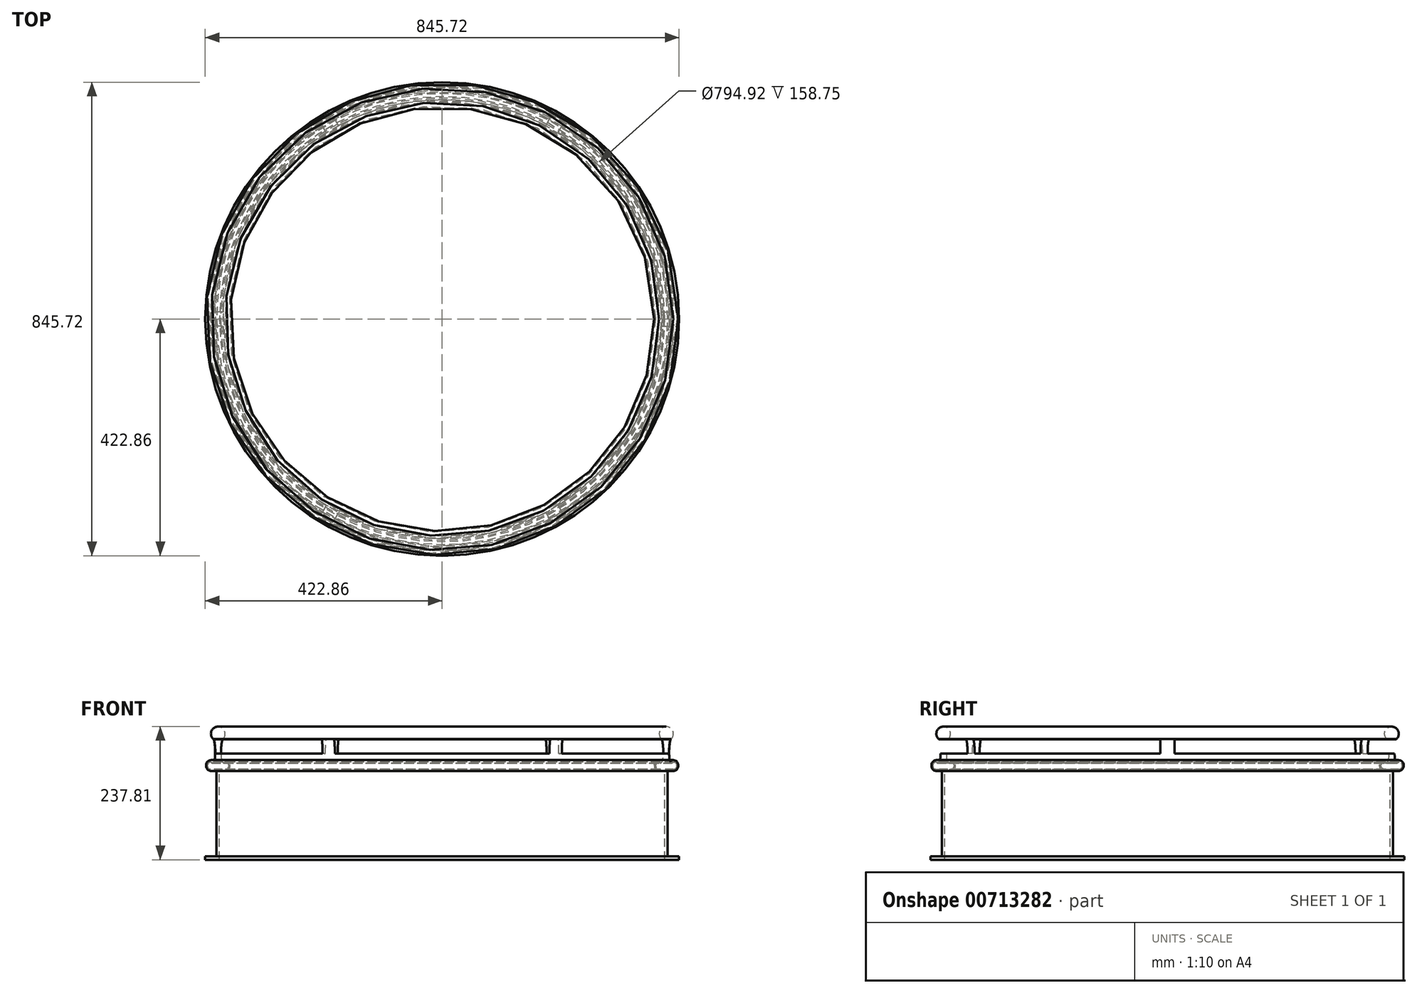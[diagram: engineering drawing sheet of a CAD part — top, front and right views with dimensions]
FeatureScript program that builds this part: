
annotation { "Feature Type Name" : "Feature", "Feature Type Description" : "" }
export const myFeature = defineFeature(function(context is Context, id is Id, definition is map)
    precondition{}
    {
        {
            var Q0;
            Q0=qCreatedBy(makeId("Front.planeOp"),FACE);
            var sketch = newSketch(context, id + "F0", { "sketchPlane" : qUnion([Q0])});
            skCircle(sketch, "E0", {"center": v(0, 0) * mm, "radius": 12.7 * mm});
            skLineSegment(sketch, "E1", {"start": v(0, -63.5) * mm, "end": v(-12.7, -63.5) * mm});
            skLineSegment(sketch, "E2", {"start": v(0, 0) * mm, "end": v(0, -63.5) * mm, "construction": true});
            skArc(sketch, "E3", {"start": v(-12.7, -50.8) * mm, "mid": v(-19.05, -57.15) * mm, "end": v(-12.7, -63.5) * mm});
            skFitSpline(sketch, "E4", {"points": [v(-12.7, -50.8) * mm, v(-9.63, -52.39) * mm, v(-6.21, -47.1) * mm, v(-8.6, -9.35) * mm], "startDerivative": vector(22.18, -25.1) * mm, "endDerivative": vector(-18.14, 18.14) * mm});
            skFitSpline(sketch, "E5", {"points": [v(-12.56, -50.43) * mm, v(-9.69, -51.96) * mm, v(-7.32, -49) * mm, v(-8.76, -47.55) * mm, v(-15.72, -47.83) * mm, v(-21.1, -53.83) * mm, v(-20.85, -60.48) * mm, v(-18.6, -64.21) * mm, v(-13.93, -66.36) * mm], "startDerivative": vector(26.86, -26.06) * mm, "endDerivative": vector(56.63, -6) * mm});
            skFitSpline(sketch, "E6", {"points": [v(-12.56, -50.43) * mm, v(-14.9, -50.8) * mm, v(-18.48, -53.57) * mm, v(-19.03, -59.46) * mm, v(-15.83, -63.1) * mm, v(-13.05, -63.82) * mm], "startDerivative": vector(-14.53, 0.11) * mm, "endDerivative": vector(20.5, -1.46) * mm});
            skLineSegment(sketch, "E7", {"start": v(-13.93, -66.36) * mm, "end": v(-2.54, -66.36) * mm});
            skLineSegment(sketch, "E8", {"start": v(-2.54, -66.36) * mm, "end": v(-2.54, -218.76) * mm});
            skLineSegment(sketch, "E9", {"start": v(-13.05, -63.82) * mm, "end": v(0, -63.82) * mm});
            skLineSegment(sketch, "E10", {"start": v(0, -58.82) * mm, "end": v(0, -76.45) * mm, "construction": true});
            skFitSpline(sketch, "E11.MirrorCS", {"points": [v(12.7, -50.8) * mm, v(9.63, -52.39) * mm, v(6.21, -47.1) * mm, v(8.6, -9.35) * mm], "startDerivative": vector(-22.18, -25.1) * mm, "endDerivative": vector(18.14, 18.14) * mm});
            skArc(sketch, "E12.MirrorCS", {"start": v(12.7, -50.8) * mm, "mid": v(19.05, -57.15) * mm, "end": v(12.7, -63.5) * mm});
            skFitSpline(sketch, "E13.MirrorCS", {"points": [v(12.56, -50.43) * mm, v(9.69, -51.96) * mm, v(7.32, -49) * mm, v(8.76, -47.55) * mm, v(15.72, -47.83) * mm, v(21.1, -53.83) * mm, v(20.85, -60.48) * mm, v(18.6, -64.21) * mm, v(13.93, -66.36) * mm], "startDerivative": vector(-26.86, -26.06) * mm, "endDerivative": vector(-56.63, -6) * mm});
            skLineSegment(sketch, "E14.MirrorCS", {"start": v(0, -63.5) * mm, "end": v(12.7, -63.5) * mm});
            skLineSegment(sketch, "E15.MirrorCS", {"start": v(13.05, -63.82) * mm, "end": v(0, -63.82) * mm});
            skLineSegment(sketch, "E16.MirrorCS", {"start": v(13.93, -66.36) * mm, "end": v(2.54, -66.36) * mm});
            skLineSegment(sketch, "E17.MirrorCS", {"start": v(2.54, -66.36) * mm, "end": v(2.54, -218.76) * mm});
            skFitSpline(sketch, "E18.MirrorCS", {"points": [v(12.56, -50.43) * mm, v(14.9, -50.8) * mm, v(18.48, -53.57) * mm, v(19.03, -59.46) * mm, v(15.83, -63.1) * mm, v(13.05, -63.82) * mm], "startDerivative": vector(14.53, 0.11) * mm, "endDerivative": vector(-20.5, -1.46) * mm});
            skLineSegment(sketch, "E19.top", {"start": v(2.54, -225.1) * mm, "end": v(-22.86, -225.1) * mm});
            skLineSegment(sketch, "E19.left", {"start": v(2.54, -218.76) * mm, "end": v(2.54, -225.1) * mm});
            skLineSegment(sketch, "E19.right", {"start": v(-22.86, -218.76) * mm, "end": v(-22.86, -225.1) * mm});
            skLineSegment(sketch, "E20.trimOffspring", {"start": v(-2.54, -218.76) * mm, "end": v(-22.86, -218.76) * mm});
            skSolve(sketch);
        }
        {
            var Q0;
            Q0=qCreatedBy(makeId("Right.planeOp"),FACE);
            cPlane(context, id + "F1", {"entities" : qUnion([Q0]), "cplaneType" : CPlaneType.OFFSET, "offset" : 400 * mm, "width" : 152.4 * mm, "height" : 152.4 * mm});
        }
        {
            var Q0;
            Q0=qCreatedBy(makeId("Front.planeOp"),FACE);
            var sketch = newSketch(context, id + "F2", { "sketchPlane" : qUnion([Q0])});
            skLineSegment(sketch, "E21", {"start": v(400, 76.37) * mm, "end": v(400, -72.94) * mm, "construction": true});
            skSolve(sketch);
        }
        {
            var Q0;
            Q0 = qSketchRegion(id + "F0", true);
            var Q1;
            Q1=sQuery(id+"F2.wireOp",EDGE,"E21");
            revolve(context, id + "F3", {"surfaceOperationType" : NewSurfaceOperationType.NEW, "entities" : qUnion([Q0]), "axis" : qUnion([Q1]), "revolveType" : RevolveType.FULL});
        }
        {
            var Q0;
            Q0=qCreatedBy(makeId("Top.planeOp"),FACE);
            cPlane(context, id + "F4", {"entities" : qUnion([Q0]), "cplaneType" : CPlaneType.OFFSET, "offset" : 10.16 * mm, "oppositeDirection" : true, "width" : 152.4 * mm, "height" : 152.4 * mm});
        }
        {
            var Q0;
            Q0=qCreatedBy(id+"F4.planeOp",FACE);
            var sketch = newSketch(context, id + "F5", { "sketchPlane" : qUnion([Q0])});
            skCircle(sketch, "E22.cCircle", {"center": v(400, 0) * mm, "radius": 439.94 * mm, "construction": true});
            skLineSegment(sketch, "E22.0", {"start": v(654, 439.94) * mm, "end": v(908, 0) * mm, "construction": true});
            skLineSegment(sketch, "E22.1", {"start": v(908, 0) * mm, "end": v(654, -439.94) * mm, "construction": true});
            skLineSegment(sketch, "E22.2", {"start": v(654, -439.94) * mm, "end": v(146, -439.94) * mm, "construction": true});
            skLineSegment(sketch, "E22.3", {"start": v(146, -439.94) * mm, "end": v(-108, 0) * mm, "construction": true});
            skLineSegment(sketch, "E22.4", {"start": v(-108, 0) * mm, "end": v(146, 439.94) * mm, "construction": true});
            skLineSegment(sketch, "E22.5", {"start": v(146, 439.94) * mm, "end": v(654, 439.94) * mm, "construction": true});
            skPoint(sketch, "E22.0.midPoint", {"position": v(781, 219.97) * mm});
            skLineSegment(sketch, "E23", {"start": v(400, 0) * mm, "end": v(-108, 0) * mm, "construction": true});
            skLineSegment(sketch, "E24", {"start": v(400, 0) * mm, "end": v(146, 439.94) * mm, "construction": true});
            skLineSegment(sketch, "E25", {"start": v(400, 0) * mm, "end": v(654, 439.94) * mm, "construction": true});
            skLineSegment(sketch, "E26", {"start": v(400, 0) * mm, "end": v(908, 0) * mm, "construction": true});
            skLineSegment(sketch, "E27", {"start": v(400, 0) * mm, "end": v(654, -439.94) * mm, "construction": true});
            skLineSegment(sketch, "E28", {"start": v(400, 0) * mm, "end": v(146, -439.94) * mm, "construction": true});
            skLineSegment(sketch, "E29.0", {"start": v(378, -12.7) * mm, "end": v(-64.81, -12.7) * mm});
            skLineSegment(sketch, "E29.1", {"start": v(378, -12.7) * mm, "end": v(156.6, -396.19) * mm});
            skLineSegment(sketch, "E30.0", {"start": v(378, 12.7) * mm, "end": v(156.6, 396.2) * mm});
            skLineSegment(sketch, "E30.1", {"start": v(378, 12.7) * mm, "end": v(-64.81, 12.7) * mm});
            skLineSegment(sketch, "E31.0", {"start": v(400, 25.4) * mm, "end": v(178.6, 408.89) * mm});
            skLineSegment(sketch, "E31.1", {"start": v(400, 25.4) * mm, "end": v(621.4, 408.9) * mm});
            skLineSegment(sketch, "E32.0", {"start": v(422, 12.7) * mm, "end": v(643.4, 396.2) * mm});
            skLineSegment(sketch, "E32.1", {"start": v(422, 12.7) * mm, "end": v(864.81, 12.7) * mm});
            skLineSegment(sketch, "E33.0", {"start": v(422, -12.7) * mm, "end": v(864.81, -12.7) * mm});
            skLineSegment(sketch, "E33.1", {"start": v(422, -12.7) * mm, "end": v(643.4, -396.2) * mm});
            skLineSegment(sketch, "E34.0", {"start": v(400, -25.4) * mm, "end": v(621.4, -408.89) * mm});
            skLineSegment(sketch, "E34.1", {"start": v(400, -25.4) * mm, "end": v(178.6, -408.9) * mm});
            skArc(sketch, "E35", {"start": v(-39.76, 12.7) * mm, "mid": v(19, 219.97) * mm, "end": v(169.12, 374.5) * mm});
            skArc(sketch, "E36", {"start": v(191.12, 387.2) * mm, "mid": v(400, 439.94) * mm, "end": v(608.88, 387.2) * mm});
            skArc(sketch, "E37", {"start": v(630.88, 374.5) * mm, "mid": v(781, 219.97) * mm, "end": v(839.76, 12.7) * mm});
            skArc(sketch, "E38", {"start": v(839.76, -12.7) * mm, "mid": v(781, -219.97) * mm, "end": v(630.88, -374.5) * mm});
            skArc(sketch, "E39", {"start": v(608.88, -387.2) * mm, "mid": v(400, -439.94) * mm, "end": v(191.12, -387.2) * mm});
            skArc(sketch, "E40", {"start": v(169.12, -374.5) * mm, "mid": v(19, -219.97) * mm, "end": v(-39.76, -12.7) * mm});
            skSolve(sketch);
        }
        {
            var Q0;
            Q0 = qSketchRegion(id + "F5", true);
            extrude(context, id + "F6", {"entities" : qUnion([Q0]), "operationType" : NewBodyOperationType.REMOVE, "oppositeDirection" : true, "depth" : 25.4 * mm, "offsetDistance" : 25.4 * mm});
        }
    });
